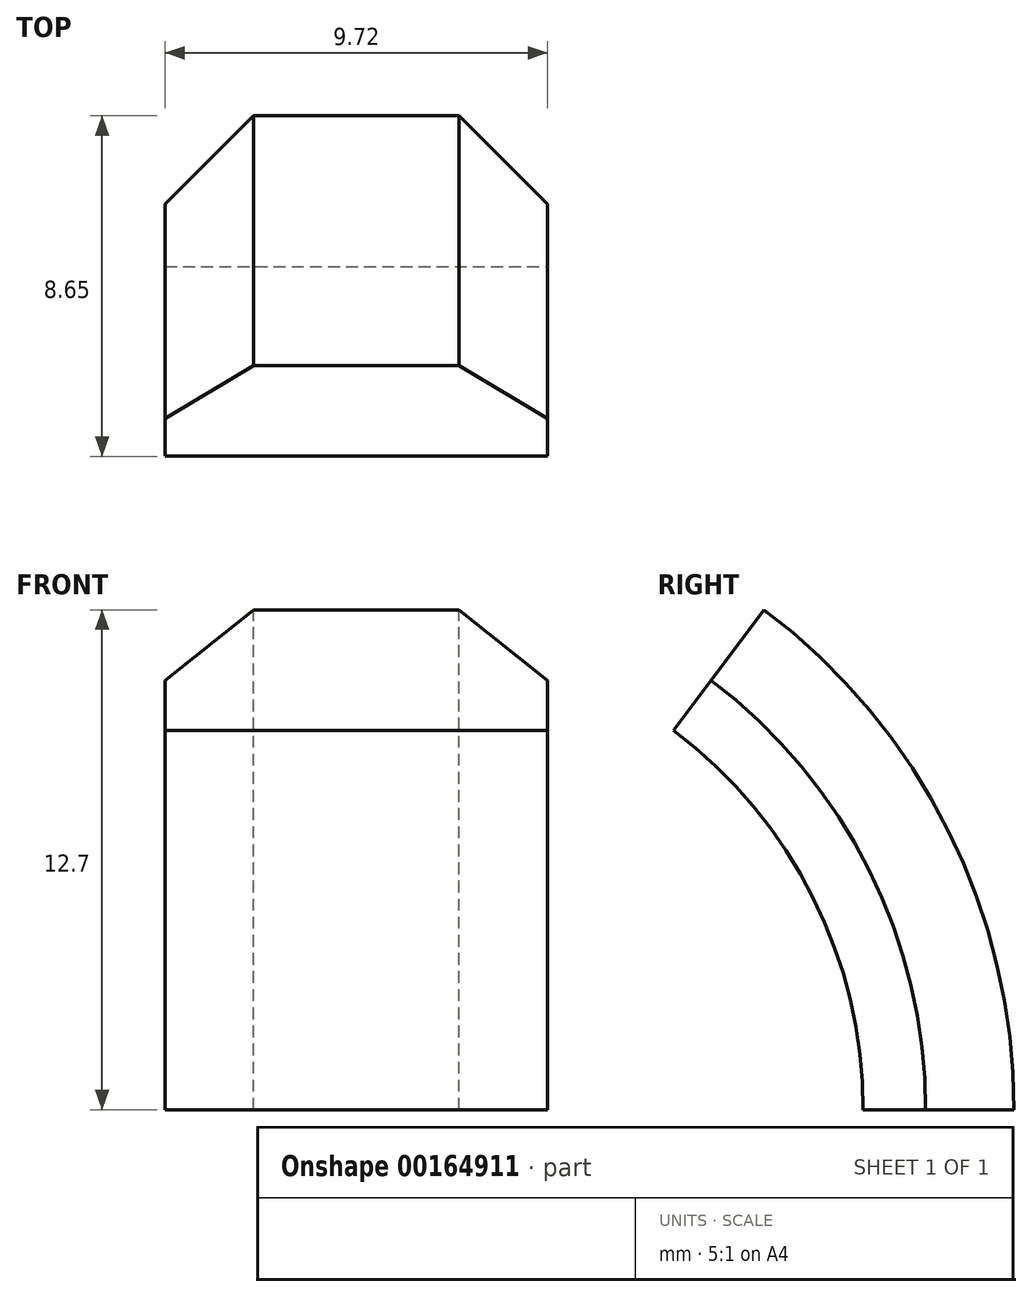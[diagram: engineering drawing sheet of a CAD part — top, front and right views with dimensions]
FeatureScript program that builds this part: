
annotation { "Feature Type Name" : "Feature", "Feature Type Description" : "" }
export const myFeature = defineFeature(function(context is Context, id is Id, definition is map)
    precondition{}
    {
        {
            var Q0;
            Q0=qCreatedBy(makeId("Top.planeOp"),FACE);
            var sketch = newSketch(context, id + "F0", { "sketchPlane" : qUnion([Q0])});
            skLineSegment(sketch, "E0", {"start": v(4.86, -2.25) * mm, "end": v(2.61, 0) * mm});
            skLineSegment(sketch, "E1", {"start": v(-2.61, 0) * mm, "end": v(-4.86, -2.25) * mm});
            skArc(sketch, "E2", {"start": v(2.61, 0) * mm, "mid": v(0, 1.08) * mm, "end": v(-2.61, 0) * mm, "construction": true});
            skLineSegment(sketch, "E3", {"start": v(-2.61, 0) * mm, "end": v(2.61, 0) * mm});
            skLineSegment(sketch, "E4", {"start": v(-4.86, -2.25) * mm, "end": v(-4.86, -3.83) * mm});
            skLineSegment(sketch, "E5", {"start": v(-4.86, -3.83) * mm, "end": v(4.86, -3.83) * mm});
            skLineSegment(sketch, "E6", {"start": v(4.86, -3.83) * mm, "end": v(4.86, -2.25) * mm});
            skSolve(sketch);
        }
        {
            var Q0;
            Q0=qCreatedBy(makeId("Right.planeOp"),FACE);
            var sketch = newSketch(context, id + "F1", { "sketchPlane" : qUnion([Q0])});
            skArc(sketch, "E7", {"start": v(0, 0) * mm, "mid": v(-1.68, 7.1) * mm, "end": v(-6.35, 12.7) * mm});
            skLineSegment(sketch, "E8", {"start": v(0, 0) * mm, "end": v(0, -9.2) * mm, "construction": true});
            skLineSegment(sketch, "E9", {"start": v(-6.35, 12.7) * mm, "end": v(-19.38, 22.47) * mm, "construction": true});
            skLineSegment(sketch, "E10", {"start": v(-6.35, 12.7) * mm, "end": v(-6.35, 0) * mm, "construction": true});
            skLineSegment(sketch, "E11", {"start": v(-6.35, 0) * mm, "end": v(0, 0) * mm, "construction": true});
            skSolve(sketch);
        }
        {
            var Q0;
            Q0=makeQuery(id+"F0.imprint","IMPRINT",FACE,{"disambiguationData":[TD([[makeQuery(id+"F0.imprint","IMPRINT",EDGE,{"derivedFrom":sQuery(id+"F0.wireOp",EDGE,"E0")}),1.0]])]});
            var Q1;
            Q1=sQuery(id+"F1.wireOp",EDGE,"E7");
            sweep(context, id + "F2", {"profiles" : qUnion([Q0]), "path" : qUnion([Q1])});
        }
    });
